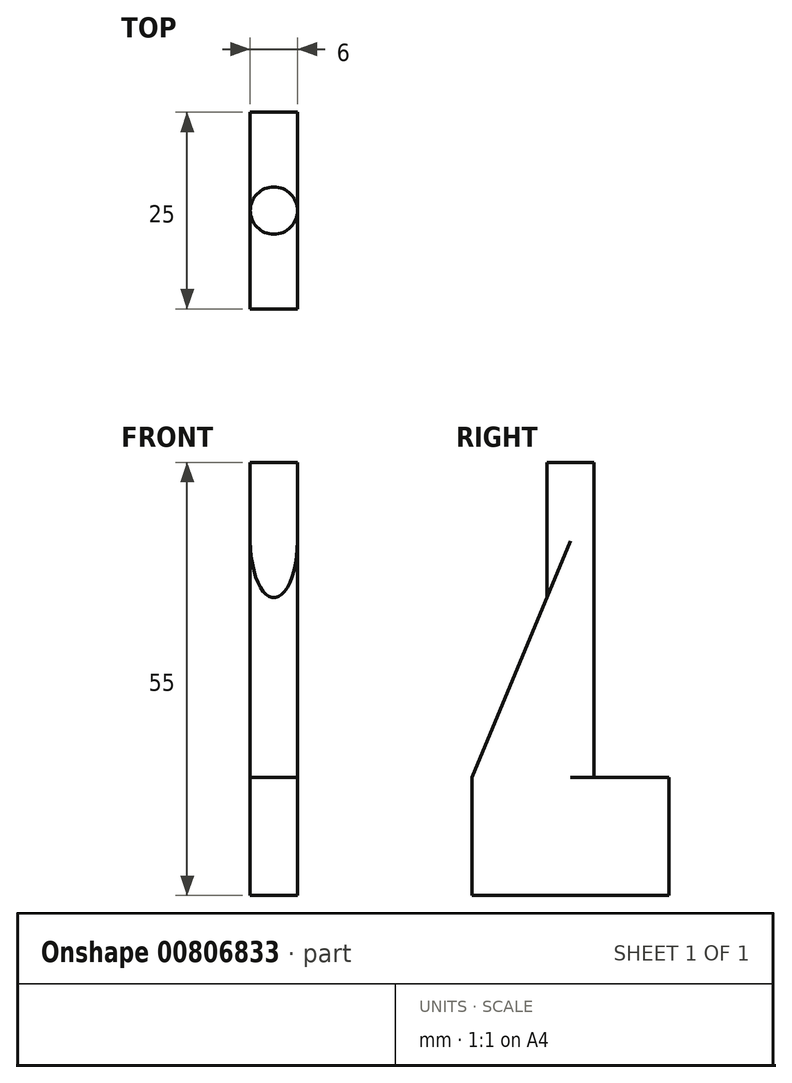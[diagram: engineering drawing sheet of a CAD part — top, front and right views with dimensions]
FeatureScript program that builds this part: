
annotation { "Feature Type Name" : "Feature", "Feature Type Description" : "" }
export const myFeature = defineFeature(function(context is Context, id is Id, definition is map)
    precondition{}
    {
        {
            var Q0;
            Q0=qCreatedBy(makeId("Top.planeOp"),FACE);
            var sketch = newSketch(context, id + "F0", { "sketchPlane" : qUnion([Q0])});
            skCircle(sketch, "E0", {"center": v(0, 0) * mm, "radius": 15 * mm});
            skCircle(sketch, "E1", {"center": v(0, 0) * mm, "radius": 3 * mm});
            skLineSegment(sketch, "E2.bottom", {"start": v(7.5, 20) * mm, "end": v(-7.5, 20) * mm});
            skLineSegment(sketch, "E2.top", {"start": v(7.5, -20) * mm, "end": v(-7.5, -20) * mm});
            skLineSegment(sketch, "E2.left", {"start": v(7.5, 20) * mm, "end": v(7.5, -20) * mm});
            skLineSegment(sketch, "E2.right", {"start": v(-7.5, 20) * mm, "end": v(-7.5, -20) * mm});
            skLineSegment(sketch, "E3.bottom", {"start": v(3, 12.5) * mm, "end": v(-3, 12.5) * mm});
            skLineSegment(sketch, "E3.top", {"start": v(3, -12.5) * mm, "end": v(-3, -12.5) * mm});
            skLineSegment(sketch, "E3.left", {"start": v(3, 12.5) * mm, "end": v(3, -12.5) * mm});
            skLineSegment(sketch, "E3.right", {"start": v(-3, 12.5) * mm, "end": v(-3, -12.5) * mm});
            skSolve(sketch);
        }
        {
            var Q0;
            Q0=makeQuery(id+"F0.imprint","IMPRINT",FACE,{"disambiguationData":[TD([[makeQuery(id+"F0.imprint","IMPRINT",EDGE,{"derivedFrom":sQuery(id+"F0.wireOp",EDGE,"E1")}),-1.0]])]});
            extrude(context, id + "F1", {"entities" : qUnion([Q0]), "depth" : 25 * mm, "offsetDistance" : 25 * mm});
        }
        {
            var Q0;
            Q0=makeQuery(id+"F0.imprint","IMPRINT",FACE,{"disambiguationData":[TD([[makeQuery(id+"F0.imprint","IMPRINT",EDGE,{"derivedFrom":sQuery(id+"F0.wireOp",EDGE,"E1")}),1.0]])]});
            extrude(context, id + "F2", {"entities" : qUnion([Q0]), "operationType" : NewBodyOperationType.ADD, "depth" : 65 * mm, "offsetDistance" : 25 * mm});
        }
        {
            var Q0;
            Q0=qCreatedBy(makeId("Right.planeOp"),FACE);
            var sketch = newSketch(context, id + "F3", { "sketchPlane" : qUnion([Q0])});
            skLineSegment(sketch, "E4", {"start": v(0, 0) * mm, "end": v(0, 25) * mm});
            skLineSegment(sketch, "E5", {"start": v(0, 25) * mm, "end": v(0, 55) * mm});
            skLineSegment(sketch, "E6", {"start": v(0, 55) * mm, "end": v(-12.5, 25) * mm});
            skLineSegment(sketch, "E7", {"start": v(-12.5, 25) * mm, "end": v(0, 25) * mm});
            skSolve(sketch);
        }
        {
            var Q0;
            Q0=qSketchRegion(id+"F3",true);
            extrude(context, id + "F4", {"entities" : qUnion([Q0]), "operationType" : NewBodyOperationType.ADD, "endBound" : BoundingType.SYMMETRIC, "depth" : 6 * mm, "offsetDistance" : 25 * mm});
        }
        {
            var Q0;
            {var subQ5=sQuery(id+"F0.wireOp",EDGE,"E3.bottom");Q0=makeQuery(id+"F0.imprint","IMPRINT",FACE,{"disambiguationData":[TD([[makeQuery(id+"F0.imprint","IMPRINT",EDGE,{"derivedFrom":subQ5}),1.0]])]});}
            var Q1;
            {var subQ0=sQuery(id+"F0.wireOp",EDGE,"E1");var subQ1=makeQuery(id+"F0.imprint","INTERSECT",VERTEX,{"derivedFrom":[subQ0,sQuery(id+"F0.wireOp",EDGE,"E3.left")]});Q1=makeQuery(id+"F0.imprint","IMPRINT",FACE,{"disambiguationData":[TD([[makeQuery(id+"F0.imprint","IMPRINT",EDGE,{"disambiguationData":[TD([[subQ1,-1.0]])],"derivedFrom":subQ0}),1.0]])]});}
            var Q2;
            {var subQ5=sQuery(id+"F0.wireOp",EDGE,"E3.top");Q2=makeQuery(id+"F0.imprint","IMPRINT",FACE,{"disambiguationData":[TD([[makeQuery(id+"F0.imprint","IMPRINT",EDGE,{"derivedFrom":subQ5}),-1.0]])]});}
            extrude(context, id + "F5", {"entities" : qUnion([Q0, Q1, Q2]), "operationType" : NewBodyOperationType.REMOVE, "oppositeDirection" : true, "depth" : -10 * mm, "offsetDistance" : 25 * mm});
        }
    });
